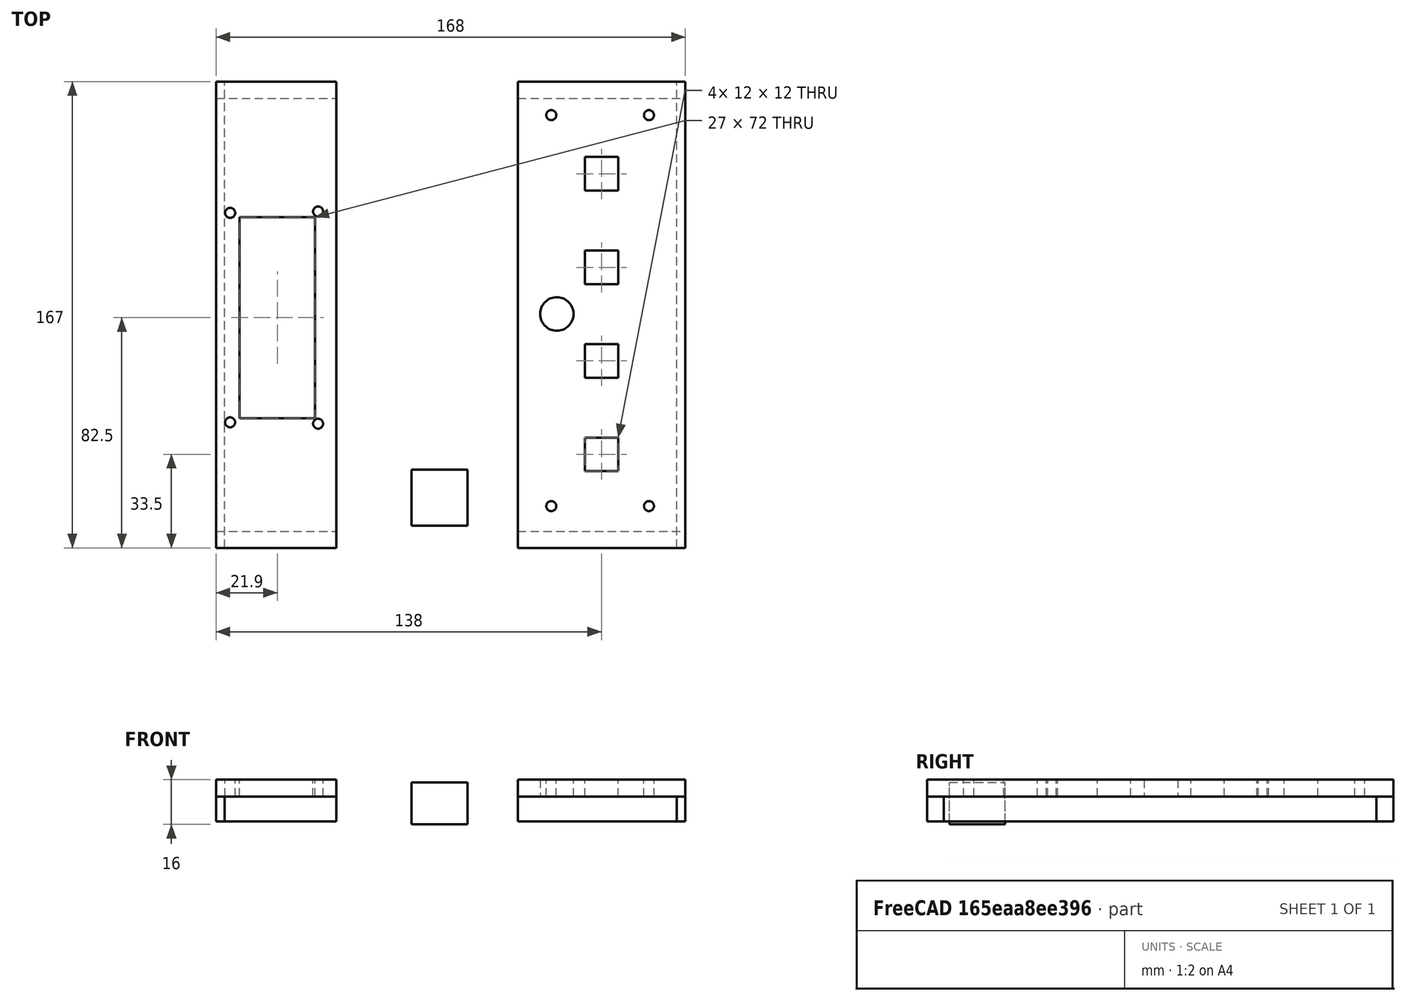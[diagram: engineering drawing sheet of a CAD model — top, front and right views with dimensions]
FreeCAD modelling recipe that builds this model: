
FCSTD DOCUMENT  (FreeCAD 0.20R29410 (Git))
Label: tapaderaV1
License: All rights reserved
LicenseURL: http://en.wikipedia.org/wiki/All_rights_reserved
objects: Part::Box×14, Part::Cut×14, Part::FeaturePython×8, Part::Cylinder×1
note: 37 computed .brp shape members not serialized (recipe doc carries the construction recipe); baked Part::Feature solids carry a one-line shape summary decoded from their .brp

FEATURE [Part::Box] Box001  label="side1"
  AttacherType = Attacher::AttachEngine3D
  Height = 9
  Length = 43
  Placement = pos=(5,0,-9) rot=(0,0,1;0rad)
  Width = 6
FEATURE [Part::Box] Box002  label="side2"
  AttacherType = Attacher::AttachEngine3D
  Height = 9
  Length = 43
  Placement = pos=(5,161,-9) rot=(0,0,1;0rad)
  Width = 6
FEATURE [Part::Box] Box003  label="side3"
  AttacherType = Attacher::AttachEngine3D
  Height = 9
  Length = 167
  Placement = pos=(8,0,-9) rot=(0,0,1;1.5708rad)
  Width = 3
FEATURE [Part::Box] Box004  label="LCD"
  AttacherType = Attacher::AttachEngine3D
  Height = 18
  Length = 27
  Placement = pos=(13.4,46.5,-10) rot=(0,0,1;0rad)
  Width = 72
FEATURE [Part::Box] Box007  label="LCD_top"
  AttacherType = Attacher::AttachEngine3D
  Height = 6
  Length = 43
  Placement = pos=(5,0,0) rot=(0,0,1;0rad)
  Width = 167
FEATURE [Part::FeaturePython] Tube005  label="screw1"  # WARN: FeaturePython — macro-defined, semantics opaque (R4)
  AttacherType = Attacher::AttachEngine3D
  Height = 20
  InnerRadius = 0
  OuterRadius = 1.8
  Placement = pos=(10,45,-10) rot=(0,0,1;0rad)
FEATURE [Part::FeaturePython] Tube006  label="screw2"  # WARN: FeaturePython — macro-defined, semantics opaque (R4)
  AttacherType = Attacher::AttachEngine3D
  Height = 20
  InnerRadius = 0
  OuterRadius = 1.8
  Placement = pos=(10,120,-10) rot=(0,0,1;0rad)
FEATURE [Part::FeaturePython] Tube007  label="screw3"  # WARN: FeaturePython — macro-defined, semantics opaque (R4)
  AttacherType = Attacher::AttachEngine3D
  Height = 20
  InnerRadius = 0
  OuterRadius = 1.8
  Placement = pos=(41.5,120.5,-10) rot=(0,0,1;0rad)
FEATURE [Part::FeaturePython] Tube008  label="screw4"  # WARN: FeaturePython — macro-defined, semantics opaque (R4)
  AttacherType = Attacher::AttachEngine3D
  Height = 21
  InnerRadius = 0
  OuterRadius = 1.8
  Placement = pos=(41.5,44.5,-13) rot=(0,0,1;0rad)
FEATURE [Part::Box] Box008  label="Buttons_top"
  AttacherType = Attacher::AttachEngine3D
  Height = 6
  Length = 60
  Placement = pos=(113,0,0) rot=(0,0,1;0rad)
  Width = 167
FEATURE [Part::Box] Box009  label="side4"
  AttacherType = Attacher::AttachEngine3D
  Height = 9
  Length = 60
  Placement = pos=(113,0,-9) rot=(0,0,1;0rad)
  Width = 6
FEATURE [Part::Box] Box010  label="side5"
  AttacherType = Attacher::AttachEngine3D
  Height = 9
  Length = 60
  Placement = pos=(113,161,-9) rot=(0,0,1;0rad)
  Width = 6
FEATURE [Part::Box] Box011  label="side6"
  AttacherType = Attacher::AttachEngine3D
  Height = 9
  Length = 167
  Placement = pos=(173,0,-9) rot=(0,0,1;1.5708rad)
  Width = 3
FEATURE [Part::FeaturePython] Tube009  label="screw5"  # WARN: FeaturePython — macro-defined, semantics opaque (R4)
  AttacherType = Attacher::AttachEngine3D
  Height = 20
  InnerRadius = 0
  OuterRadius = 1.8
  Placement = pos=(125,15,-10) rot=(0,0,1;0rad)
FEATURE [Part::FeaturePython] Tube010  label="screw6"  # WARN: FeaturePython — macro-defined, semantics opaque (R4)
  AttacherType = Attacher::AttachEngine3D
  Height = 20
  InnerRadius = 0
  OuterRadius = 1.8
  Placement = pos=(160,15,-10) rot=(0,0,1;0rad)
FEATURE [Part::FeaturePython] Tube011  label="screw7"  # WARN: FeaturePython — macro-defined, semantics opaque (R4)
  AttacherType = Attacher::AttachEngine3D
  Height = 20
  InnerRadius = 0
  OuterRadius = 1.8
  Placement = pos=(160,155,-10) rot=(0,0,1;0rad)
FEATURE [Part::FeaturePython] Tube012  label="screw8"  # WARN: FeaturePython — macro-defined, semantics opaque (R4)
  AttacherType = Attacher::AttachEngine3D
  Height = 20
  InnerRadius = 0
  OuterRadius = 1.8
  Placement = pos=(125,155,-10) rot=(0,0,1;0rad)
FEATURE [Part::Box] Box012  label="Button1"
  AttacherType = Attacher::AttachEngine3D
  Height = 10
  Length = 12
  Placement = pos=(137,27.5,-2) rot=(0,0,1;0rad)
  Width = 12
FEATURE [Part::Box] Box013  label="Button4"
  AttacherType = Attacher::AttachEngine3D
  Height = 10
  Length = 12
  Placement = pos=(137,128,-2) rot=(0,0,1;0rad)
  Width = 12
FEATURE [Part::Box] Box014  label="Button3"
  AttacherType = Attacher::AttachEngine3D
  Height = 10
  Length = 12
  Placement = pos=(137,94.5,-2) rot=(0,0,1;0rad)
  Width = 12
FEATURE [Part::Box] Box015  label="Button2"
  AttacherType = Attacher::AttachEngine3D
  Height = 10
  Length = 12
  Placement = pos=(137,61,-2) rot=(0,0,1;0rad)
  Width = 12
FEATURE [Part::Cylinder] Cylinder005  label="Buzzer"
  Angle = 360
  AttacherType = Attacher::AttachEngine3D
  FirstAngle = 0
  Height = 10
  Placement = pos=(127,83.8,-2) rot=(0,0,1;0rad)
  Radius = 6
  SecondAngle = 0
FEATURE [Part::Cut] Cut
  Base = -> Box007
  Tool = -> Box004
FEATURE [Part::Cut] Cut001
  Base = -> Cut
  Tool = -> Tube005
FEATURE [Part::Cut] Cut002
  Base = -> Cut001
  Tool = -> Tube006
FEATURE [Part::Cut] Cut003
  Base = -> Cut002
  Tool = -> Tube007
FEATURE [Part::Cut] Cut004
  Base = -> Cut003
  Tool = -> Tube008
FEATURE [Part::Cut] Cut005
  Base = -> Box008
  Tool = -> Tube009
FEATURE [Part::Cut] Cut006
  Base = -> Cut005
  Tool = -> Cylinder005
FEATURE [Part::Cut] Cut007
  Base = -> Cut006
  Tool = -> Box015
FEATURE [Part::Cut] Cut008
  Base = -> Cut007
  Tool = -> Box013
FEATURE [Part::Cut] Cut009
  Base = -> Cut008
  Tool = -> Box012
FEATURE [Part::Cut] Cut010
  Base = -> Cut009
  Tool = -> Box014
FEATURE [Part::Cut] Cut011
  Base = -> Cut010
  Tool = -> Tube012
FEATURE [Part::Cut] Cut012
  Base = -> Cut011
  Tool = -> Tube011
FEATURE [Part::Cut] Cut013
  Base = -> Cut012
  Tool = -> Tube010
FEATURE [Part::Box] Box  label="LedMatrix_supports"
  AttacherType = Attacher::AttachEngine3D
  Height = 15
  Length = 20
  Placement = pos=(75,8,-10) rot=(0,0,1;0rad)
  Width = 20
